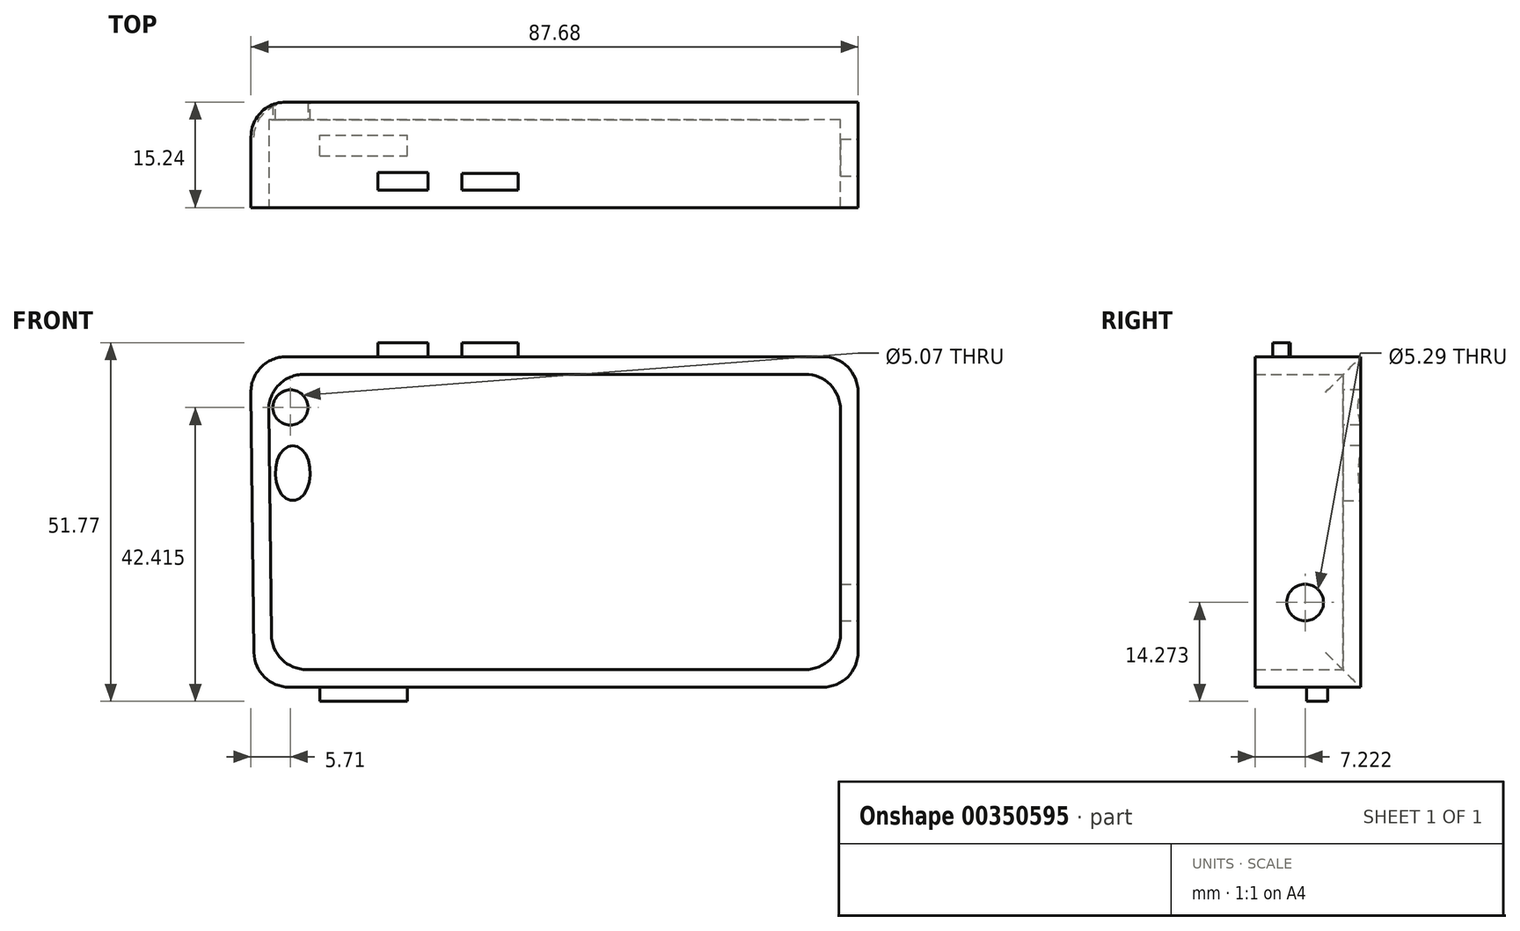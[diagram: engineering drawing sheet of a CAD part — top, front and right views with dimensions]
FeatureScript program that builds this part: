
annotation { "Feature Type Name" : "Feature", "Feature Type Description" : "" }
export const myFeature = defineFeature(function(context is Context, id is Id, definition is map)
    precondition{}
    {
        {
            var Q0;
            Q0=qCreatedBy(makeId("Front.planeOp"),FACE);
            var sketch = newSketch(context, id + "F0", { "sketchPlane" : qUnion([Q0])});
            skLineSegment(sketch, "E0", {"start": v(-50.54, 37.34) * mm, "end": v(37.2, 37.34) * mm});
            skLineSegment(sketch, "E1", {"start": v(37.2, 37.34) * mm, "end": v(37.2, -10.36) * mm});
            skLineSegment(sketch, "E2", {"start": v(37.2, -10.36) * mm, "end": v(-49.97, -10.36) * mm});
            skLineSegment(sketch, "E3", {"start": v(-49.97, -10.36) * mm, "end": v(-50.54, 37.34) * mm});
            skSolve(sketch);
        }
        {
            var Q0;
            Q0=makeQuery(id+"F0.imprint","IMPRINT",FACE,{"disambiguationData":[TD([[makeQuery(id+"F0.imprint","IMPRINT",EDGE,{"derivedFrom":sQuery(id+"F0.wireOp",EDGE,"E0")}),-1.0]])]});
            extrude(context, id + "F1", {"entities" : qUnion([Q0]), "endBound" : BoundingType.SYMMETRIC, "depth" : 25.4 * mm});
        }
        {
            var Q0;
            Q0=makeQuery(id+"F1.opExtrude","CAP_FACE",FACE,{"disambiguationData":[OSD([sQuery(id+"F0.wireOp",EDGE,"E0"),sQuery(id+"F0.wireOp",EDGE,"E1"),sQuery(id+"F0.wireOp",EDGE,"E2"),sQuery(id+"F0.wireOp",EDGE,"E3")])],"isStart":false});
            shell(context, id + "F2", {"entities" : qUnion([Q0]), "thickness" : 2.54 * mm});
        }
        {
            var Q0;
            Q0=makeQuery(id+"F2.opShell","OFFSET_FACE",FACE,{"disambiguationData":[OSD([sQuery(id+"F0.wireOp",EDGE,"E0"),sQuery(id+"F0.wireOp",EDGE,"E1"),sQuery(id+"F0.wireOp",EDGE,"E2"),sQuery(id+"F0.wireOp",EDGE,"E3")])]});
            var sketch = newSketch(context, id + "F3", { "sketchPlane" : qUnion([Q0])});
            skCircle(sketch, "E4", {"center": v(-44.77, 30.01) * mm, "radius": 2.53 * mm});
            skSolve(sketch);
        }
        {
            var Q0;
            Q0=makeQuery(id+"F3.imprint","IMPRINT",FACE,{"disambiguationData":[TD([[makeQuery(id+"F3.imprint","IMPRINT",EDGE,{"derivedFrom":sQuery(id+"F3.wireOp",EDGE,"E4")}),1.0]])]});
            extrude(context, id + "F4", {"entities" : qUnion([Q0]), "operationType" : NewBodyOperationType.REMOVE, "oppositeDirection" : true, "depth" : 25.4 * mm});
        }
        {
            var Q0;
            Q0=makeQuery(id+"F1.opExtrude","SWEPT_FACE",FACE,{"disambiguationData":[OSD([sQuery(id+"F0.wireOp",EDGE,"E2")])]});
            var sketch = newSketch(context, id + "F5", { "sketchPlane" : qUnion([Q0])});
            skLineSegment(sketch, "E5.bottom", {"start": v(-40.56, -4.92) * mm, "end": v(-27.9, -4.92) * mm});
            skLineSegment(sketch, "E5.top", {"start": v(-40.56, -7.93) * mm, "end": v(-27.9, -7.93) * mm});
            skLineSegment(sketch, "E5.left", {"start": v(-40.56, -4.92) * mm, "end": v(-40.56, -7.93) * mm});
            skLineSegment(sketch, "E5.right", {"start": v(-27.9, -4.92) * mm, "end": v(-27.9, -7.93) * mm});
            skSolve(sketch);
        }
        {
            var Q0;
            Q0=makeQuery(id+"F5.imprint","IMPRINT",FACE,{"disambiguationData":[TD([[makeQuery(id+"F5.imprint","IMPRINT",EDGE,{"derivedFrom":sQuery(id+"F5.wireOp",EDGE,"E5.bottom")}),-1.0]])]});
            extrude(context, id + "F6", {"entities" : qUnion([Q0]), "operationType" : NewBodyOperationType.ADD, "depth" : 2.03 * mm});
        }
        {
            var Q0;
            Q0=makeQuery(id+"F1.opExtrude","SWEPT_EDGE",EDGE,{"disambiguationData":[OSD([sQuery(id+"F0.wireOp",EDGE,"E0"),sQuery(id+"F0.wireOp",EDGE,"E3")])]});
            var Q1;
            Q1=makeQuery(id+"F1.opExtrude","CAP_EDGE",EDGE,{"disambiguationData":[OSD([sQuery(id+"F0.wireOp",EDGE,"E3")])],"isStart":true});
            var Q2;
            Q2=makeQuery(id+"F1.opExtrude","SWEPT_EDGE",EDGE,{"disambiguationData":[OSD([sQuery(id+"F0.wireOp",EDGE,"E2"),sQuery(id+"F0.wireOp",EDGE,"E3")])]});
            var Q3;
            Q3=makeQuery(id+"F1.opExtrude","SWEPT_EDGE",EDGE,{"disambiguationData":[OSD([sQuery(id+"F0.wireOp",EDGE,"E1"),sQuery(id+"F0.wireOp",EDGE,"E2")])]});
            var Q4;
            Q4=makeQuery(id+"F1.opExtrude","SWEPT_EDGE",EDGE,{"disambiguationData":[OSD([sQuery(id+"F0.wireOp",EDGE,"E0"),sQuery(id+"F0.wireOp",EDGE,"E1")])]});
            fillet(context, id + "F7", {"entities" : qUnion([Q0, Q1, Q2, Q3, Q4]), "radius" : 5.08 * mm, "tangentPropagation" : true, "allowEdgeOverflow" : false});
        }
        {
            var Q0;
            Q0=makeQuery(id+"F1.opExtrude","SWEPT_FACE",FACE,{"disambiguationData":[OSD([sQuery(id+"F0.wireOp",EDGE,"E0")])]});
            var sketch = newSketch(context, id + "F8", { "sketchPlane" : qUnion([Q0])});
            skLineSegment(sketch, "E6.bottom", {"start": v(-32.15, 0) * mm, "end": v(-24.89, 0) * mm});
            skLineSegment(sketch, "E6.top", {"start": v(-32.15, 2.55) * mm, "end": v(-24.89, 2.55) * mm});
            skLineSegment(sketch, "E6.left", {"start": v(-32.15, 0) * mm, "end": v(-32.15, 2.55) * mm});
            skLineSegment(sketch, "E6.right", {"start": v(-24.89, 0) * mm, "end": v(-24.89, 2.55) * mm});
            skLineSegment(sketch, "E7.bottom", {"start": v(-19.99, 0) * mm, "end": v(-11.89, 0) * mm});
            skLineSegment(sketch, "E7.top", {"start": v(-19.99, 2.38) * mm, "end": v(-11.89, 2.38) * mm});
            skLineSegment(sketch, "E7.left", {"start": v(-19.99, 0) * mm, "end": v(-19.99, 2.38) * mm});
            skLineSegment(sketch, "E7.right", {"start": v(-11.89, 0) * mm, "end": v(-11.89, 2.38) * mm});
            skSolve(sketch);
        }
        {
            var Q0;
            Q0=qSketchRegion(id+"F8",true);
            extrude(context, id + "F9", {"entities" : qUnion([Q0]), "operationType" : NewBodyOperationType.ADD, "depth" : 2.03 * mm});
        }
        {
            var Q0;
            Q0=makeQuery(id+"F2.opShell","OFFSET_FACE",FACE,{"disambiguationData":[OSD([sQuery(id+"F0.wireOp",EDGE,"E0"),sQuery(id+"F0.wireOp",EDGE,"E1"),sQuery(id+"F0.wireOp",EDGE,"E2"),sQuery(id+"F0.wireOp",EDGE,"E3")])]});
            var sketch = newSketch(context, id + "F10", { "sketchPlane" : qUnion([Q0])});
            skEllipse(sketch, "E8", {"center": v(-44.43, 20.55) * mm, "majorRadius": 3.98 * mm, "minorRadius": 2.52 * mm, "majorAxis": v(0, 1)});
            skSolve(sketch);
        }
        {
            var Q0;
            Q0=makeQuery(id+"F10.imprint","IMPRINT",FACE,{"disambiguationData":[TD([[makeQuery(id+"F10.imprint","IMPRINT",EDGE,{"derivedFrom":sQuery(id+"F10.wireOp",EDGE,"E8")}),1.0]])]});
            extrude(context, id + "F11", {"entities" : qUnion([Q0]), "operationType" : NewBodyOperationType.REMOVE, "oppositeDirection" : true, "depth" : 5.33 * mm});
        }
        {
            var Q0;
            Q0=makeQuery(id+"F1.opExtrude","CAP_FACE",FACE,{"disambiguationData":[OSD([sQuery(id+"F0.wireOp",EDGE,"E0"),sQuery(id+"F0.wireOp",EDGE,"E1"),sQuery(id+"F0.wireOp",EDGE,"E2"),sQuery(id+"F0.wireOp",EDGE,"E3")])],"isStart":false});
            extrude(context, id + "F12", {"entities" : qUnion([Q0]), "operationType" : NewBodyOperationType.REMOVE, "oppositeDirection" : true, "depth" : 10.16 * mm});
        }
        {
            var Q0;
            Q0=makeQuery(id+"F2.opShell","OFFSET_EDGE",EDGE,{"disambiguationData":[OSD([sQuery(id+"F0.wireOp",EDGE,"E2"),sQuery(id+"F0.wireOp",EDGE,"E3")])]});
            var Q1;
            Q1=makeQuery(id+"F2.opShell","OFFSET_EDGE",EDGE,{"disambiguationData":[OSD([sQuery(id+"F0.wireOp",EDGE,"E0"),sQuery(id+"F0.wireOp",EDGE,"E3")])]});
            var Q2;
            Q2=makeQuery(id+"F2.opShell","OFFSET_EDGE",EDGE,{"disambiguationData":[OSD([sQuery(id+"F0.wireOp",EDGE,"E1"),sQuery(id+"F0.wireOp",EDGE,"E2")])]});
            var Q3;
            Q3=makeQuery(id+"F2.opShell","OFFSET_EDGE",EDGE,{"disambiguationData":[OSD([sQuery(id+"F0.wireOp",EDGE,"E0"),sQuery(id+"F0.wireOp",EDGE,"E1")])]});
            fillet(context, id + "F13", {"entities" : qUnion([Q0, Q1, Q2, Q3]), "radius" : 5.08 * mm, "tangentPropagation" : true, "allowEdgeOverflow" : false});
        }
        {
            var Q0;
            Q0=makeQuery(id+"F1.opExtrude","SWEPT_FACE",FACE,{"disambiguationData":[OSD([sQuery(id+"F0.wireOp",EDGE,"E1")])]});
            var sketch = newSketch(context, id + "F14", { "sketchPlane" : qUnion([Q0])});
            skCircle(sketch, "E9", {"center": v(4.68, 1.87) * mm, "radius": 2.64 * mm});
            skSolve(sketch);
        }
        {
            var Q0;
            Q0=makeQuery(id+"F14.imprint","IMPRINT",FACE,{"disambiguationData":[TD([[makeQuery(id+"F14.imprint","IMPRINT",EDGE,{"derivedFrom":sQuery(id+"F14.wireOp",EDGE,"E9")}),1.0]])]});
            extrude(context, id + "F15", {"entities" : qUnion([Q0]), "operationType" : NewBodyOperationType.REMOVE, "oppositeDirection" : true, "depth" : 25.4 * mm});
        }
    });
